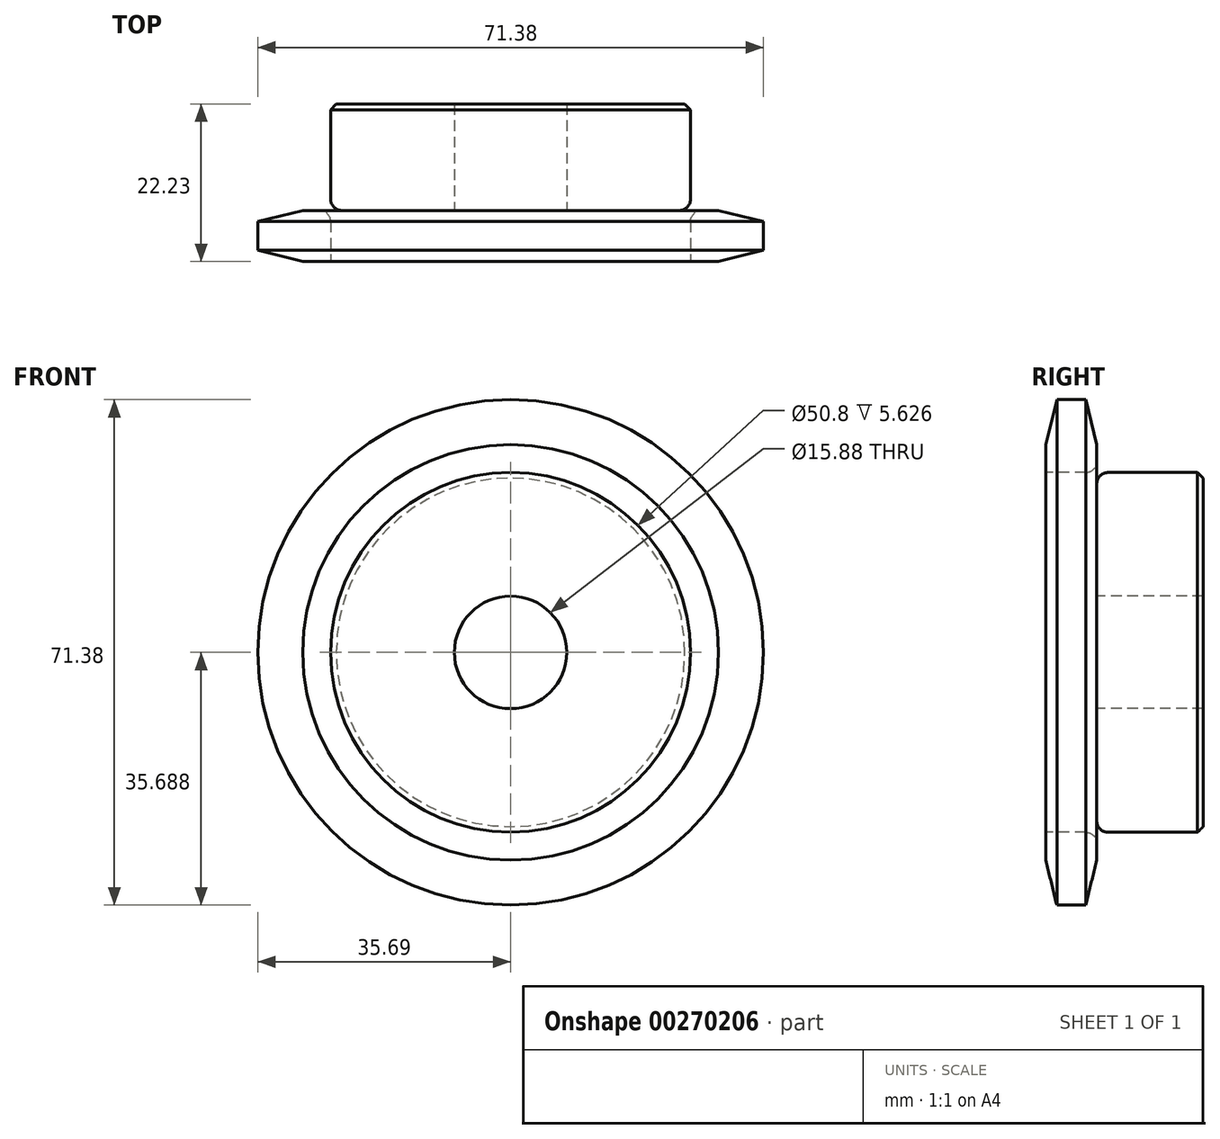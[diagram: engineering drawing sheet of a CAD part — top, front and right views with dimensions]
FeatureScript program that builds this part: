
annotation { "Feature Type Name" : "Feature", "Feature Type Description" : "" }
export const myFeature = defineFeature(function(context is Context, id is Id, definition is map)
    precondition{}
    {
        {
            var Q0;
            Q0=qCreatedBy(makeId("Right.planeOp"),FACE);
            var sketch = newSketch(context, id + "F0", { "sketchPlane" : qUnion([Q0])});
            skLineSegment(sketch, "E0", {"start": v(-46.89, 36.56) * mm, "end": v(-24.66, 36.56) * mm});
            skLineSegment(sketch, "E1.bottom", {"start": v(-46.89, 44.5) * mm, "end": v(-39.67, 44.5) * mm});
            skLineSegment(sketch, "E1.top", {"start": v(-46.89, 72.25) * mm, "end": v(-39.67, 72.25) * mm});
            skLineSegment(sketch, "E1.left", {"start": v(-46.89, 44.5) * mm, "end": v(-46.89, 72.25) * mm});
            skLineSegment(sketch, "E1.right", {"start": v(-39.67, 44.5) * mm, "end": v(-39.67, 72.25) * mm});
            skLineSegment(sketch, "E2.bottom", {"start": v(-46.89, 44.5) * mm, "end": v(-24.66, 44.5) * mm});
            skLineSegment(sketch, "E2.top", {"start": v(-46.89, 61.96) * mm, "end": v(-24.66, 61.96) * mm});
            skLineSegment(sketch, "E2.left", {"start": v(-46.89, 44.5) * mm, "end": v(-46.89, 61.96) * mm});
            skLineSegment(sketch, "E2.right", {"start": v(-24.66, 44.5) * mm, "end": v(-24.66, 61.96) * mm});
            skLineSegment(sketch, "E3.MirrorCS", {"start": v(-46.89, 11.16) * mm, "end": v(-24.66, 11.16) * mm});
            skLineSegment(sketch, "E4.MirrorCS", {"start": v(-46.89, 28.62) * mm, "end": v(-39.67, 28.62) * mm});
            skLineSegment(sketch, "E5.MirrorCS", {"start": v(-46.89, 0.87) * mm, "end": v(-39.67, 0.87) * mm});
            skLineSegment(sketch, "E6.MirrorCS", {"start": v(-46.89, 28.62) * mm, "end": v(-46.89, 0.87) * mm});
            skLineSegment(sketch, "E7.MirrorCS", {"start": v(-39.67, 28.62) * mm, "end": v(-39.67, 0.87) * mm});
            skLineSegment(sketch, "E8.MirrorCS", {"start": v(-46.89, 28.62) * mm, "end": v(-24.66, 28.62) * mm});
            skLineSegment(sketch, "E9.MirrorCS", {"start": v(-46.89, 28.62) * mm, "end": v(-46.89, 11.16) * mm});
            skLineSegment(sketch, "E10.MirrorCS", {"start": v(-24.66, 28.62) * mm, "end": v(-24.66, 11.16) * mm});
            skSolve(sketch);
        }
        {
            var Q0;
            {var subQ0=sQuery(id+"F0.wireOp",EDGE,"E1.top");Q0=makeQuery(id+"F0.imprint","IMPRINT",FACE,{"disambiguationData":[TD([[makeQuery(id+"F0.imprint","IMPRINT",EDGE,{"derivedFrom":subQ0}),-1.0]])]});}
            var Q1;
            {var subQ5=sQuery(id+"F0.wireOp",EDGE,"E2.left");Q1=makeQuery(id+"F0.imprint","IMPRINT",FACE,{"disambiguationData":[TD([[makeQuery(id+"F0.imprint","IMPRINT",EDGE,{"derivedFrom":subQ5}),-1.0]])]});}
            var Q2;
            {var subQ5=sQuery(id+"F0.wireOp",EDGE,"E2.right");Q2=makeQuery(id+"F0.imprint","IMPRINT",FACE,{"disambiguationData":[TD([[makeQuery(id+"F0.imprint","IMPRINT",EDGE,{"derivedFrom":subQ5}),1.0]])]});}
            var Q3;
            Q3=sQuery(id+"F0.wireOp",EDGE,"E0");
            revolve(context, id + "F1", {"entities" : qUnion([Q0, Q1, Q2]), "axis" : qUnion([Q3]), "revolveType" : RevolveType.FULL});
        }
        {
            var Q0;
            Q0=makeQuery(id+"F1.opRevolve","SWEPT_EDGE",EDGE,{"disambiguationData":[OSD([sQuery(id+"F0.wireOp",EDGE,"E1.right"),sQuery(id+"F0.wireOp",EDGE,"E2.top")])]});
            fillet(context, id + "F2", {"entities" : qUnion([Q0]), "radius" : 1.59 * mm, "tangentPropagation" : true, "allowEdgeOverflow" : false});
        }
        {
            var Q0;
            Q0=makeQuery(id+"F1.opRevolve","SWEPT_EDGE",EDGE,{"disambiguationData":[OSD([sQuery(id+"F0.wireOp",EDGE,"E2.top"),sQuery(id+"F0.wireOp",EDGE,"E2.right")])]});
            chamfer(context, id + "F3", {"entities" : qUnion([Q0]), "width" : 0.8 * mm, "tangentPropagation" : true});
        }
        {
            var Q0;
            Q0=makeQuery(id+"F1.opRevolve","SWEPT_EDGE",EDGE,{"disambiguationData":[OSD([sQuery(id+"F0.wireOp",EDGE,"E1.top"),sQuery(id+"F0.wireOp",EDGE,"E1.left")])]});
            var Q1;
            Q1=makeQuery(id+"F1.opRevolve","SWEPT_EDGE",EDGE,{"disambiguationData":[OSD([sQuery(id+"F0.wireOp",EDGE,"E1.top"),sQuery(id+"F0.wireOp",EDGE,"E1.right")])]});
            chamfer(context, id + "F4", {"entities" : qUnion([Q0, Q1]), "chamferType" : ChamferType.TWO_OFFSETS, "width1" : 6.35 * mm, "oppositeDirection" : false, "width2" : 1.57 * mm, "tangentPropagation" : true});
        }
    });
